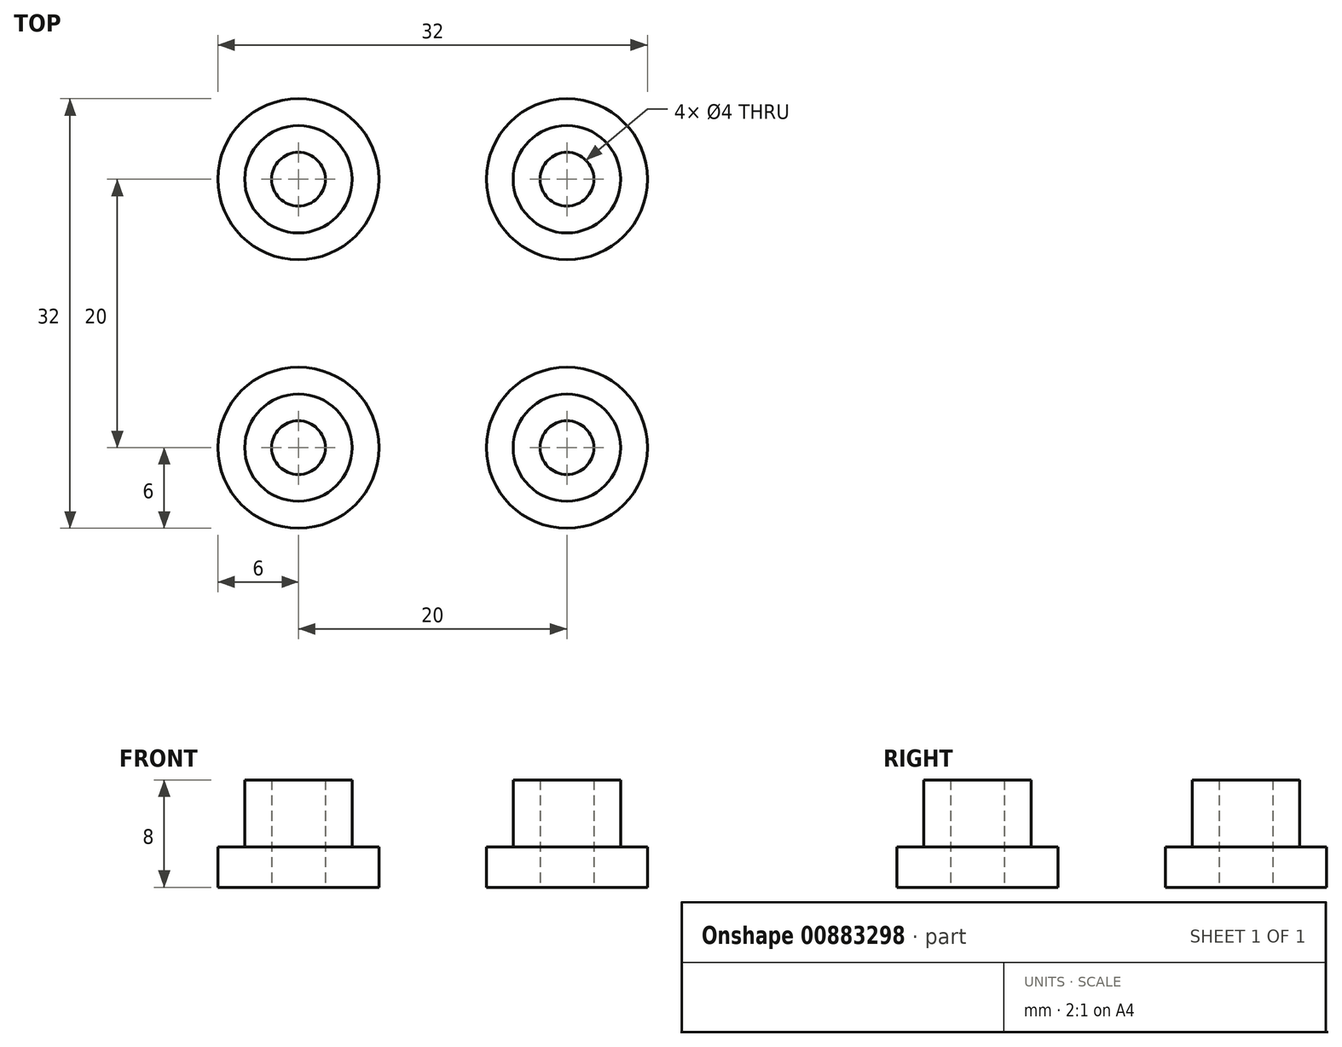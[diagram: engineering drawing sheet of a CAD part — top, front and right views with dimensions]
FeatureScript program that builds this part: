
annotation { "Feature Type Name" : "Feature", "Feature Type Description" : "" }
export const myFeature = defineFeature(function(context is Context, id is Id, definition is map)
    precondition{}
    {
        {
            var Q0;
            Q0=qCreatedBy(makeId("Top.planeOp"),FACE);
            var sketch = newSketch(context, id + "F0", { "sketchPlane" : qUnion([Q0])});
            skCircle(sketch, "E0", {"center": v(0, 0) * mm, "radius": 2 * mm});
            skCircle(sketch, "E1", {"center": v(0, 0) * mm, "radius": 4 * mm});
            skCircle(sketch, "E2", {"center": v(0, 0) * mm, "radius": 6 * mm});
            skSolve(sketch);
        }
        {
            var Q0;
            Q0=makeQuery(id+"F0.imprint","IMPRINT",FACE,{"disambiguationData":[TD([[makeQuery(id+"F0.imprint","IMPRINT",EDGE,{"derivedFrom":sQuery(id+"F0.wireOp",EDGE,"E0")}),-1.0]])]});
            extrude(context, id + "F1", {"entities" : qUnion([Q0]), "depth" : 8 * mm, "offsetDistance" : 25 * mm});
        }
        {
            var Q0;
            Q0=makeQuery(id+"F0.imprint","IMPRINT",FACE,{"disambiguationData":[TD([[makeQuery(id+"F0.imprint","IMPRINT",EDGE,{"derivedFrom":sQuery(id+"F0.wireOp",EDGE,"E1")}),-1.0]])]});
            extrude(context, id + "F2", {"entities" : qUnion([Q0]), "operationType" : NewBodyOperationType.ADD, "depth" : 3 * mm, "offsetDistance" : 25 * mm});
        }
        {
            var Q0;
            Q0=makeQuery(id+"F1.opExtrude","SWEPT_BODY",BODY,{"disambiguationData":[OSD([sQuery(id+"F0.wireOp",EDGE,"E0"),sQuery(id+"F0.wireOp",EDGE,"E1")])]});
            transform(context, id + "F3", {"entities" : qUnion([Q0]), "transformType" : TransformType.TRANSLATION_3D, "dx" : 20 * mm, "dy" : 0 * mm, "dz" : 0 * mm, "makeCopy" : true});
        }
        {
            var Q0;
            Q0=makeQuery(id+"F3.opPattern","COPY",BODY,{"derivedFrom":makeQuery(id+"F1.opExtrude","SWEPT_BODY",BODY,{"disambiguationData":[OSD([sQuery(id+"F0.wireOp",EDGE,"E0"),sQuery(id+"F0.wireOp",EDGE,"E1")])]}),"instanceName":"1"});
            var Q1;
            Q1=makeQuery(id+"F1.opExtrude","SWEPT_BODY",BODY,{"disambiguationData":[OSD([sQuery(id+"F0.wireOp",EDGE,"E0"),sQuery(id+"F0.wireOp",EDGE,"E1")])]});
            transform(context, id + "F4", {"entities" : qUnion([Q0, Q1]), "transformType" : TransformType.TRANSLATION_3D, "dx" : 0 * mm, "dy" : 20 * mm, "dz" : 0 * mm, "makeCopy" : true});
        }
    });
